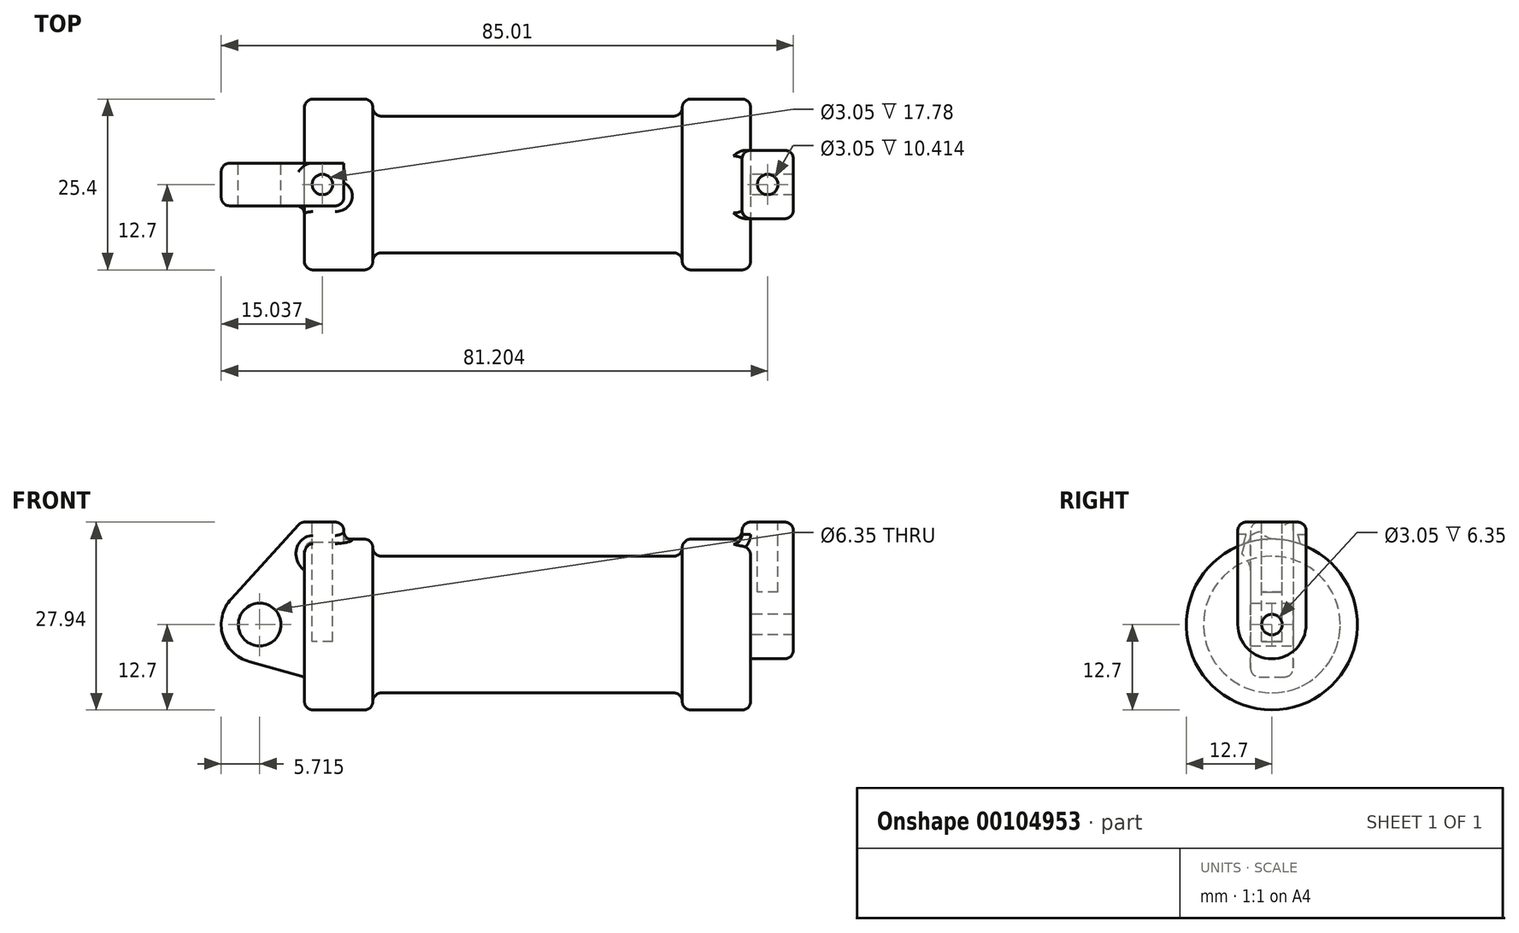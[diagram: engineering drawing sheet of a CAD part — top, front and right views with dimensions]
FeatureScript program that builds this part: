
annotation { "Feature Type Name" : "Feature", "Feature Type Description" : "" }
export const myFeature = defineFeature(function(context is Context, id is Id, definition is map)
    precondition{}
    {
        {
            var Q0;
            Q0=qCreatedBy(makeId("Front.planeOp"),FACE);
            var sketch = newSketch(context, id + "F0", { "sketchPlane" : qUnion([Q0])});
            skLineSegment(sketch, "E0", {"start": v(0, 0) * mm, "end": v(0, 12.7) * mm});
            skLineSegment(sketch, "E1", {"start": v(0, 12.7) * mm, "end": v(10.16, 12.7) * mm});
            skLineSegment(sketch, "E2", {"start": v(10.16, 12.7) * mm, "end": v(10.16, 10.16) * mm});
            skLineSegment(sketch, "E3", {"start": v(10.16, 10.16) * mm, "end": v(56.13, 10.16) * mm});
            skLineSegment(sketch, "E4", {"start": v(56.13, 10.16) * mm, "end": v(56.13, 12.7) * mm});
            skLineSegment(sketch, "E5", {"start": v(56.13, 12.7) * mm, "end": v(66.3, 12.7) * mm});
            skLineSegment(sketch, "E6", {"start": v(66.3, 12.7) * mm, "end": v(66.3, 0) * mm});
            skLineSegment(sketch, "E7", {"start": v(66.3, 0) * mm, "end": v(0, 0) * mm});
            skLineSegment(sketch, "E8", {"start": v(5.84, 15.24) * mm, "end": v(-0.5, 15.24) * mm});
            skLineSegment(sketch, "E9", {"start": v(-0.5, 15.24) * mm, "end": v(-10.88, 3.85) * mm});
            skLineSegment(sketch, "E10", {"start": v(0, 0) * mm, "end": v(-6.65, 0) * mm});
            skCircle(sketch, "E11", {"center": v(-6.65, 0) * mm, "radius": 5.72 * mm});
            skCircle(sketch, "E12", {"center": v(-6.65, 0) * mm, "radius": 3.18 * mm});
            skLineSegment(sketch, "E13", {"start": v(5.84, 15.24) * mm, "end": v(5.84, -9.4) * mm});
            skLineSegment(sketch, "E14", {"start": v(5.84, -9.4) * mm, "end": v(-8.18, -5.5) * mm});
            skSolve(sketch);
        }
        {
            var Q0;
            {var subQ0=sQuery(id+"F0.wireOp",EDGE,"E2");Q0=makeQuery(id+"F0.imprint","IMPRINT",FACE,{"disambiguationData":[TD([[makeQuery(id+"F0.imprint","IMPRINT",EDGE,{"derivedFrom":subQ0}),-1.0]])]});}
            var Q1;
            {var subQ0=sQuery(id+"F0.wireOp",EDGE,"E0");Q1=makeQuery(id+"F0.imprint","IMPRINT",FACE,{"disambiguationData":[TD([[makeQuery(id+"F0.imprint","IMPRINT",EDGE,{"derivedFrom":subQ0}),-1.0]])]});}
            var Q2;
            Q2=sQuery(id+"F0.wireOp",EDGE,"E7");
            revolve(context, id + "F1", {"entities" : qUnion([Q0, Q1]), "axis" : qUnion([Q2]), "revolveType" : RevolveType.FULL});
        }
        {
            var Q0;
            {var subQ3=sQuery(id+"F0.wireOp",EDGE,"E0");Q0=makeQuery(id+"F0.imprint","IMPRINT",FACE,{"disambiguationData":[TD([[makeQuery(id+"F0.imprint","IMPRINT",EDGE,{"derivedFrom":subQ3}),1.0]])]});}
            var Q1;
            {var subQ4=sQuery(id+"F0.wireOp",EDGE,"E12");Q1=makeQuery(id+"F0.imprint","IMPRINT",FACE,{"disambiguationData":[TD([[makeQuery(id+"F0.imprint","IMPRINT",EDGE,{"derivedFrom":subQ4}),-1.0]])]});}
            var Q2;
            {var subQ0=sQuery(id+"F0.wireOp",EDGE,"E14");Q2=makeQuery(id+"F0.imprint","IMPRINT",FACE,{"disambiguationData":[TD([[makeQuery(id+"F0.imprint","IMPRINT",EDGE,{"derivedFrom":subQ0}),-1.0]])]});}
            var Q3;
            {var subQ0=sQuery(id+"F0.wireOp",EDGE,"E0");Q3=makeQuery(id+"F0.imprint","IMPRINT",FACE,{"disambiguationData":[TD([[makeQuery(id+"F0.imprint","IMPRINT",EDGE,{"derivedFrom":subQ0}),-1.0]])]});}
            extrude(context, id + "F2", {"entities" : qUnion([Q0, Q1, Q2, Q3]), "operationType" : NewBodyOperationType.ADD, "endBound" : BoundingType.SYMMETRIC, "depth" : 6.35 * mm});
        }
        {
            var Q0;
            Q0=makeQuery(id+"F1.opRevolve","SWEPT_FACE",FACE,{"disambiguationData":[OSD([sQuery(id+"F0.wireOp",EDGE,"E6")])]});
            var sketch = newSketch(context, id + "F3", { "sketchPlane" : qUnion([Q0])});
            skCircle(sketch, "E15", {"center": v(0, 0) * mm, "radius": 1.52 * mm});
            skCircle(sketch, "E16", {"center": v(0, 0) * mm, "radius": 5.08 * mm});
            skLineSegment(sketch, "E17", {"start": v(5.08, 0) * mm, "end": v(5.08, 15.24) * mm});
            skLineSegment(sketch, "E18", {"start": v(-5.08, 0) * mm, "end": v(-5.08, 15.24) * mm});
            skLineSegment(sketch, "E19", {"start": v(-5.08, 15.24) * mm, "end": v(5.08, 15.24) * mm});
            skSolve(sketch);
        }
        {
            var Q0;
            Q0=makeQuery(id+"F3.imprint","IMPRINT",FACE,{"disambiguationData":[TD([[makeQuery(id+"F3.imprint","IMPRINT",EDGE,{"derivedFrom":sQuery(id+"F3.wireOp",EDGE,"E15")}),-1.0]])]});
            var Q1;
            {var subQ0=sQuery(id+"F3.wireOp",EDGE,"E17");var subQ1=sQuery(id+"F3.wireOp",EDGE,"E16");var subQ2=makeQuery(id+"F3.imprint","INTERSECT",VERTEX,{"derivedFrom":[subQ1,subQ0]});Q1=makeQuery(id+"F3.imprint","IMPRINT",FACE,{"disambiguationData":[TD([[makeQuery(id+"F3.imprint","IMPRINT",EDGE,{"disambiguationData":[TD([[subQ2,-1.0]])],"derivedFrom":subQ1}),-1.0]])]});}
            var Q2;
            {var subQ0=sQuery(id+"F3.wireOp",EDGE,"E19");Q2=makeQuery(id+"F3.imprint","IMPRINT",FACE,{"disambiguationData":[TD([[makeQuery(id+"F3.imprint","IMPRINT",EDGE,{"derivedFrom":subQ0}),-1.0]])]});}
            extrude(context, id + "F4", {"entities" : qUnion([Q0, Q1, Q2]), "operationType" : NewBodyOperationType.ADD, "depth" : 6.35 * mm, "hasSecondDirection" : true, "secondDirectionOppositeDirection" : true, "secondDirectionDepth" : 1.27 * mm});
        }
        {
            var Q0;
            Q0=makeQuery(id+"F2.opExtrude","SWEPT_FACE",FACE,{"disambiguationData":[OSD([sQuery(id+"F0.wireOp",EDGE,"E8")])]});
            var sketch = newSketch(context, id + "F5", { "sketchPlane" : qUnion([Q0])});
            skCircle(sketch, "E20", {"center": v(2.67, 0) * mm, "radius": 1.52 * mm});
            skPoint(sketch, "E20.centerSnap0", {"position": v(2.67, -3.18) * mm});
            skPoint(sketch, "E20.centerSnap1", {"position": v(-0.5, 0) * mm});
            skSolve(sketch);
        }
        {
            var Q0;
            Q0=makeQuery(id+"F5.imprint","IMPRINT",FACE,{"disambiguationData":[TD([[makeQuery(id+"F5.imprint","IMPRINT",EDGE,{"derivedFrom":sQuery(id+"F5.wireOp",EDGE,"E20")}),1.0]])]});
            extrude(context, id + "F6", {"entities" : qUnion([Q0]), "operationType" : NewBodyOperationType.REMOVE, "oppositeDirection" : true, "depth" : 17.78 * mm});
        }
        {
            var Q0;
            Q0=makeQuery(id+"F4.opExtrude","SWEPT_FACE",FACE,{"disambiguationData":[OSD([sQuery(id+"F3.wireOp",EDGE,"E19")])]});
            var sketch = newSketch(context, id + "F7", { "sketchPlane" : qUnion([Q0])});
            skCircle(sketch, "E21", {"center": v(68.83, 0) * mm, "radius": 1.52 * mm});
            skPoint(sketch, "E21.centerSnap0", {"position": v(72.64, 0) * mm});
            skPoint(sketch, "E21.centerSnap1", {"position": v(68.83, -5.08) * mm});
            skSolve(sketch);
        }
        {
            var Q0;
            Q0=makeQuery(id+"F7.imprint","IMPRINT",FACE,{"disambiguationData":[TD([[makeQuery(id+"F7.imprint","IMPRINT",EDGE,{"derivedFrom":sQuery(id+"F7.wireOp",EDGE,"E21")}),1.0]])]});
            extrude(context, id + "F8", {"entities" : qUnion([Q0]), "operationType" : NewBodyOperationType.REMOVE, "oppositeDirection" : true, "depth" : 10.4 * mm});
        }
        {
            var Q0;
            Q0=makeQuery(id+"F2.opExtrude","CAP_EDGE",EDGE,{"disambiguationData":[OSD([sQuery(id+"F0.wireOp",EDGE,"E9")])],"isStart":false});
            var Q1;
            Q1=makeQuery(id+"F2.opExtrude","CAP_EDGE",EDGE,{"disambiguationData":[OSD([sQuery(id+"F0.wireOp",EDGE,"E8")])],"isStart":false});
            var Q2;
            Q2=makeQuery(id+"F2.opExtrude","CAP_EDGE",EDGE,{"disambiguationData":[OSD([sQuery(id+"F0.wireOp",EDGE,"E13")])],"isStart":false});
            var Q3;
            Q3=makeQuery(id+"F2.boolean.opBoolean","INTERSECT",EDGE,{"derivedFrom":[makeQuery(id+"F1.opRevolve","SWEPT_FACE",FACE,{"disambiguationData":[OSD([sQuery(id+"F0.wireOp",EDGE,"E1")])]}),makeQuery(id+"F2.opExtrude","CAP_FACE",FACE,{"disambiguationData":[OSD([sQuery(id+"F0.wireOp",EDGE,"E8"),sQuery(id+"F0.wireOp",EDGE,"E9"),sQuery(id+"F0.wireOp",EDGE,"E11"),sQuery(id+"F0.wireOp",EDGE,"E12"),sQuery(id+"F0.wireOp",EDGE,"E13"),sQuery(id+"F0.wireOp",EDGE,"E14")])],"isStart":false})]});
            var Q4;
            Q4=makeQuery(id+"F1.opRevolve","SWEPT_EDGE",EDGE,{"disambiguationData":[OSD([sQuery(id+"F0.wireOp",EDGE,"E0"),sQuery(id+"F0.wireOp",EDGE,"E1")])]});
            var Q5;
            Q5=makeQuery(id+"F2.opExtrude","SWEPT_EDGE",EDGE,{"disambiguationData":[OSD([sQuery(id+"F0.wireOp",EDGE,"E8"),sQuery(id+"F0.wireOp",EDGE,"E13")])]});
            var Q6;
            Q6=makeQuery(id+"F1.opRevolve","SWEPT_EDGE",EDGE,{"disambiguationData":[OSD([sQuery(id+"F0.wireOp",EDGE,"E1"),sQuery(id+"F0.wireOp",EDGE,"E2")])]});
            var Q7;
            Q7=makeQuery(id+"F1.opRevolve","SWEPT_EDGE",EDGE,{"disambiguationData":[OSD([sQuery(id+"F0.wireOp",EDGE,"E2"),sQuery(id+"F0.wireOp",EDGE,"E3")])]});
            var Q8;
            Q8=makeQuery(id+"F2.opExtrude","CAP_EDGE",EDGE,{"disambiguationData":[OSD([sQuery(id+"F0.wireOp",EDGE,"E9")])],"isStart":true});
            var Q9;
            Q9=makeQuery(id+"F2.opExtrude","SWEPT_EDGE",EDGE,{"disambiguationData":[OSD([sQuery(id+"F0.wireOp",EDGE,"E8"),sQuery(id+"F0.wireOp",EDGE,"E9")])]});
            var Q10;
            Q10=makeQuery(id+"F1.opRevolve","SWEPT_EDGE",EDGE,{"disambiguationData":[OSD([sQuery(id+"F0.wireOp",EDGE,"E3"),sQuery(id+"F0.wireOp",EDGE,"E4")])]});
            var Q11;
            Q11=makeQuery(id+"F1.opRevolve","SWEPT_EDGE",EDGE,{"disambiguationData":[OSD([sQuery(id+"F0.wireOp",EDGE,"E4"),sQuery(id+"F0.wireOp",EDGE,"E5")])]});
            var Q12;
            Q12=makeQuery(id+"F4.boolean.opBoolean","INTERSECT",EDGE,{"derivedFrom":[makeQuery(id+"F1.opRevolve","SWEPT_FACE",FACE,{"disambiguationData":[OSD([sQuery(id+"F0.wireOp",EDGE,"E5")])]}),makeQuery(id+"F4.opExtrude","CAP_FACE",FACE,{"disambiguationData":[OSD([sQuery(id+"F3.wireOp",EDGE,"E15"),sQuery(id+"F3.wireOp",EDGE,"E16"),sQuery(id+"F3.wireOp",EDGE,"E17"),sQuery(id+"F3.wireOp",EDGE,"E18"),sQuery(id+"F3.wireOp",EDGE,"E19")])],"isStart":true})]});
            var Q13;
            Q13=makeQuery(id+"F4.opExtrude","CAP_EDGE",EDGE,{"disambiguationData":[OSD([sQuery(id+"F3.wireOp",EDGE,"E19")])],"isStart":true});
            var Q14;
            Q14=makeQuery(id+"F1.opRevolve","SWEPT_EDGE",EDGE,{"disambiguationData":[OSD([sQuery(id+"F0.wireOp",EDGE,"E5"),sQuery(id+"F0.wireOp",EDGE,"E6")])]});
            fillet(context, id + "F9", {"entities" : qUnion([Q0, Q1, Q2, Q3, Q4, Q5, Q6, Q7, Q8, Q9, Q10, Q11, Q12, Q13, Q14]), "radius" : 1.27 * mm, "tangentPropagation" : true, "allowEdgeOverflow" : false});
        }
        {
            var Q0;
            Q0=makeQuery(id+"F4.opExtrude","SWEPT_EDGE",EDGE,{"disambiguationData":[OSD([sQuery(id+"F3.wireOp",EDGE,"E18"),sQuery(id+"F3.wireOp",EDGE,"E19")])]});
            var Q1;
            Q1=makeQuery(id+"F4.opExtrude","CAP_EDGE",EDGE,{"disambiguationData":[OSD([sQuery(id+"F3.wireOp",EDGE,"E18")])],"isStart":false});
            var Q2;
            Q2=makeQuery(id+"F4.opExtrude","CAP_EDGE",EDGE,{"disambiguationData":[OSD([sQuery(id+"F3.wireOp",EDGE,"E19")])],"isStart":false});
            var Q3;
            Q3=makeQuery(id+"F4.opExtrude","SWEPT_EDGE",EDGE,{"disambiguationData":[OSD([sQuery(id+"F3.wireOp",EDGE,"E17"),sQuery(id+"F3.wireOp",EDGE,"E19")])]});
            fillet(context, id + "F10", {"entities" : qUnion([Q0, Q1, Q2, Q3]), "radius" : 1.27 * mm, "tangentPropagation" : true, "allowEdgeOverflow" : false});
        }
    });
